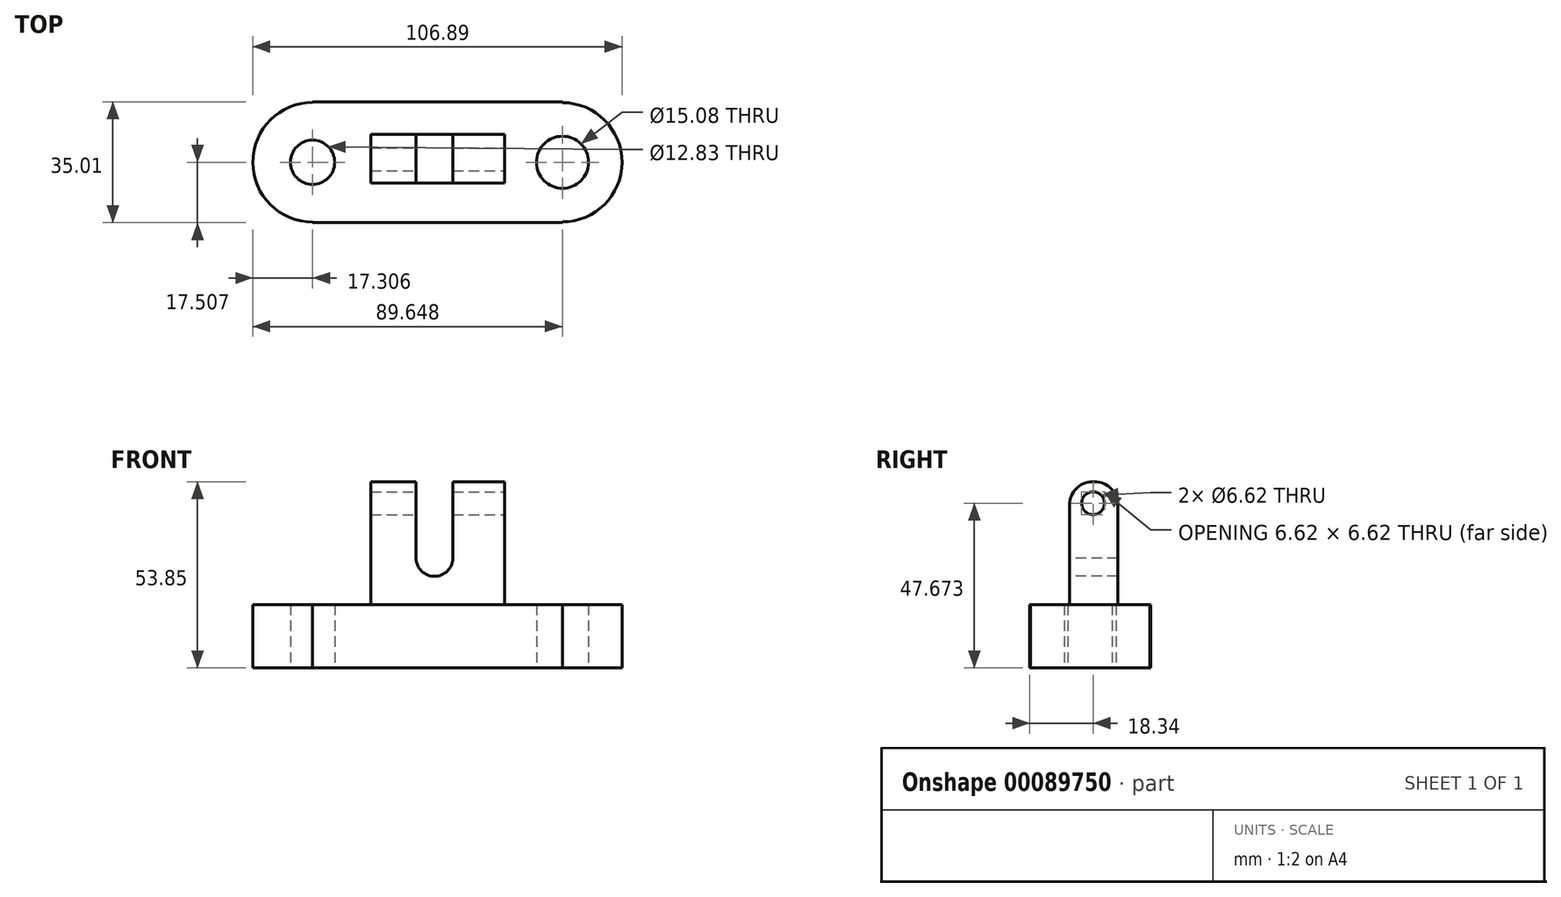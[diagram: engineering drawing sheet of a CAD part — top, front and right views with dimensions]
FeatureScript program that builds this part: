
annotation { "Feature Type Name" : "Feature", "Feature Type Description" : "" }
export const myFeature = defineFeature(function(context is Context, id is Id, definition is map)
    precondition{}
    {
        {
            var Q0;
            Q0=qCreatedBy(makeId("Top.planeOp"),FACE);
            var sketch = newSketch(context, id + "F0", { "sketchPlane" : qUnion([Q0])});
            skLineSegment(sketch, "E0.bottom", {"start": v(-35, 16.67) * mm, "end": v(37.34, 16.67) * mm});
            skLineSegment(sketch, "E0.top", {"start": v(-35, -18.34) * mm, "end": v(37.34, -18.34) * mm});
            skLineSegment(sketch, "E0.left", {"start": v(-35, 16.67) * mm, "end": v(-35, -18.34) * mm});
            skLineSegment(sketch, "E0.right", {"start": v(37.34, 16.67) * mm, "end": v(37.34, -18.34) * mm});
            skCircle(sketch, "E1", {"center": v(-35, -0.83) * mm, "radius": 17.3 * mm});
            skCircle(sketch, "E2", {"center": v(37.34, -0.83) * mm, "radius": 17.25 * mm});
            skCircle(sketch, "E3", {"center": v(-35, -0.83) * mm, "radius": 6.41 * mm});
            skCircle(sketch, "E4", {"center": v(37.34, -0.83) * mm, "radius": 7.54 * mm});
            skSolve(sketch);
        }
        {
            var Q0;
            {var subQ1=sQuery(id+"F0.wireOp",EDGE,"E0.bottom");Q0=makeQuery(id+"F0.imprint","IMPRINT",FACE,{"disambiguationData":[TD([[makeQuery(id+"F0.imprint","IMPRINT",EDGE,{"derivedFrom":subQ1}),-1.0]])]});}
            var Q1;
            {var subQ0=sQuery(id+"F0.wireOp",EDGE,"E2");var subQ1=sQuery(id+"F0.wireOp",EDGE,"E0.right");var subQ2=makeQuery(id+"F0.imprint","INTERSECT",VERTEX,{"disambiguationData":[OD(0.0)],"derivedFrom":[subQ1,subQ0]});Q1=makeQuery(id+"F0.imprint","IMPRINT",FACE,{"disambiguationData":[TD([[makeQuery(id+"F0.imprint","IMPRINT",EDGE,{"disambiguationData":[TD([[subQ2,-1.0]])],"derivedFrom":subQ1}),1.0]])]});}
            var Q2;
            {var subQ0=sQuery(id+"F0.wireOp",EDGE,"E1");var subQ1=sQuery(id+"F0.wireOp",EDGE,"E0.left");var subQ2=makeQuery(id+"F0.imprint","INTERSECT",VERTEX,{"disambiguationData":[OD(0.0)],"derivedFrom":[subQ1,subQ0]});Q2=makeQuery(id+"F0.imprint","IMPRINT",FACE,{"disambiguationData":[TD([[makeQuery(id+"F0.imprint","IMPRINT",EDGE,{"disambiguationData":[TD([[subQ2,-1.0]])],"derivedFrom":subQ1}),-1.0]])]});}
            var Q3;
            {var subQ0=sQuery(id+"F0.wireOp",EDGE,"E1");var subQ1=sQuery(id+"F0.wireOp",EDGE,"E0.left");var subQ2=makeQuery(id+"F0.imprint","INTERSECT",VERTEX,{"disambiguationData":[OD(0.0)],"derivedFrom":[subQ1,subQ0]});Q3=makeQuery(id+"F0.imprint","IMPRINT",FACE,{"disambiguationData":[TD([[makeQuery(id+"F0.imprint","IMPRINT",EDGE,{"disambiguationData":[TD([[subQ2,-1.0]])],"derivedFrom":subQ1}),1.0]])]});}
            var Q4;
            {var subQ0=sQuery(id+"F0.wireOp",EDGE,"E2");var subQ1=sQuery(id+"F0.wireOp",EDGE,"E0.right");var subQ2=makeQuery(id+"F0.imprint","INTERSECT",VERTEX,{"disambiguationData":[OD(0.0)],"derivedFrom":[subQ1,subQ0]});Q4=makeQuery(id+"F0.imprint","IMPRINT",FACE,{"disambiguationData":[TD([[makeQuery(id+"F0.imprint","IMPRINT",EDGE,{"disambiguationData":[TD([[subQ2,-1.0]])],"derivedFrom":subQ1}),-1.0]])]});}
            extrude(context, id + "F1", {"entities" : qUnion([Q0, Q1, Q2, Q3, Q4]), "depth" : 18.29 * mm});
        }
        {
            var Q0;
            Q0=qCreatedBy(makeId("Top.planeOp"),FACE);
            cPlane(context, id + "F2", {"entities" : qUnion([Q0]), "cplaneType" : CPlaneType.OFFSET, "offset" : 18.29 * mm, "width" : 152.4 * mm, "height" : 152.4 * mm});
        }
        {
            var Q0;
            Q0=qCreatedBy(id+"F2.planeOp",FACE);
            var sketch = newSketch(context, id + "F3", { "sketchPlane" : qUnion([Q0])});
            skLineSegment(sketch, "E5.bottom", {"start": v(-18.12, 7.19) * mm, "end": v(20.57, 7.19) * mm});
            skLineSegment(sketch, "E5.top", {"start": v(-18.12, -6.85) * mm, "end": v(20.57, -6.85) * mm});
            skLineSegment(sketch, "E5.left", {"start": v(-18.12, 7.19) * mm, "end": v(-18.12, -6.85) * mm});
            skLineSegment(sketch, "E5.right", {"start": v(20.57, 7.19) * mm, "end": v(20.57, -6.85) * mm});
            skSolve(sketch);
        }
        {
            var Q0;
            Q0 = qSketchRegion(id + "F3", true);
            extrude(context, id + "F4", {"entities" : qUnion([Q0]), "operationType" : NewBodyOperationType.ADD, "depth" : 35.56 * mm});
        }
        {
            var Q0;
            Q0=makeQuery(id+"F4.opExtrude","CAP_EDGE",EDGE,{"disambiguationData":[OSD([sQuery(id+"F3.wireOp",EDGE,"E5.top")])],"isStart":false});
            fillet(context, id + "F5", {"entities" : qUnion([Q0]), "radius" : 6.76 * mm, "tangentPropagation" : true, "allowEdgeOverflow" : false});
        }
        {
            var Q0;
            Q0=makeQuery(id+"F4.opExtrude","CAP_EDGE",EDGE,{"disambiguationData":[OSD([sQuery(id+"F3.wireOp",EDGE,"E5.bottom")])],"isStart":false});
            fillet(context, id + "F6", {"entities" : qUnion([Q0]), "radius" : 6.75 * mm, "tangentPropagation" : true, "allowEdgeOverflow" : false});
        }
        {
            var Q0;
            Q0=qCreatedBy(makeId("Front.planeOp"),FACE);
            cPlane(context, id + "F7", {"entities" : qUnion([Q0]), "cplaneType" : CPlaneType.OFFSET, "offset" : 14.73 * mm, "width" : 152.4 * mm, "height" : 152.4 * mm});
        }
        {
            var Q0;
            Q0=qCreatedBy(id+"F7.planeOp",FACE);
            var sketch = newSketch(context, id + "F8", { "sketchPlane" : qUnion([Q0])});
            skLineSegment(sketch, "E6.bottom", {"start": v(-5.09, 53.87) * mm, "end": v(5.63, 53.87) * mm});
            skLineSegment(sketch, "E6.top", {"start": v(-5.09, 31.8) * mm, "end": v(5.63, 31.8) * mm});
            skLineSegment(sketch, "E6.left", {"start": v(-5.09, 53.87) * mm, "end": v(-5.09, 31.8) * mm});
            skLineSegment(sketch, "E6.right", {"start": v(5.63, 53.87) * mm, "end": v(5.63, 31.8) * mm});
            skCircle(sketch, "E7", {"center": v(0.27, 31.8) * mm, "radius": 5.3 * mm});
            skSolve(sketch);
        }
        {
            var Q0;
            Q0 = qSketchRegion(id + "F8", true);
            extrude(context, id + "F9", {"entities" : qUnion([Q0]), "operationType" : NewBodyOperationType.REMOVE, "oppositeDirection" : true, "depth" : 51.56 * mm});
        }
        {
            var Q0;
            Q0=qCreatedBy(makeId("Right.planeOp"),FACE);
            cPlane(context, id + "F10", {"entities" : qUnion([Q0]), "cplaneType" : CPlaneType.OFFSET, "offset" : 25.4 * mm, "width" : 152.4 * mm, "height" : 152.4 * mm});
        }
        {
            var Q0;
            Q0=qCreatedBy(id+"F10.planeOp",FACE);
            var sketch = newSketch(context, id + "F11", { "sketchPlane" : qUnion([Q0])});
            skCircle(sketch, "E8", {"center": v(0, 47.67) * mm, "radius": 3.31 * mm});
            skSolve(sketch);
        }
        {
            var Q0;
            Q0 = qSketchRegion(id + "F11", true);
            extrude(context, id + "F12", {"entities" : qUnion([Q0]), "operationType" : NewBodyOperationType.REMOVE, "oppositeDirection" : true, "depth" : 139.95 * mm});
        }
    });
